# Revit family: a904765e-5bd2-4ae0-a95b-f6b34d1ab062
name_source: partatom
category: Pipe Fittings
revit_build: Autodesk Revit 2016 (Build: 20161004_0715(x64)
units: mm (PartAtom-declared; Revit-internal decimal feet)

## family parameters
Always vertical = Yes
Cut with Voids When Loaded = No
OmniClass Number = 23.45.05.14.11.17
OmniClass Title = Shower/Bath Seats
Part Type = Elbow
Round Connector Dimension = Use Diameter
Shared = No
Work Plane-Based = No

## types (1)
- Bathtub Seat
    04 CSI = 10 28 00
    95 CSI = 10800
    Architectural Design Manual = www.inprocorp.com/Products/Details.aspx?ProductId=463#downloads
    Arm Length = 1' - 6 1/2"
    Assembly Code = C1030200
    Bath Seat = PVC - InPro - White
    Default Elevation = 3' - 0"
    Depth = 0' - 6 5/16"
    Description = Removable & Width Adjustable
    HPD and EPD URL = https://www.inprocorp.com
    Height = 3' - 0"
    Ivory = Yes
    Length = 2' - 2"
    Length_Seat = 1' - 0 1/2"
    Manufacturer = Inpro
    Masterformat Number = 10.28.16
    Masterformat Title = Bath Accessories
    Model = DSGBRWBS-IVRY
    Revisions Date = 03/26/2010
    SMARTBIM Object Version = 3
    Series = Triton
    Special Color = No
    Subcategory = Bath & Toilet Accessories
    Type Comments = Bathtub Seat
    URL = www.inprocorp.com
    White = No
    Width = 1' - 0 1/2"

## geometry (parser evidence)
native form markers: Blend x2, Sweep x3
no freeform markers — native parametric forms only
